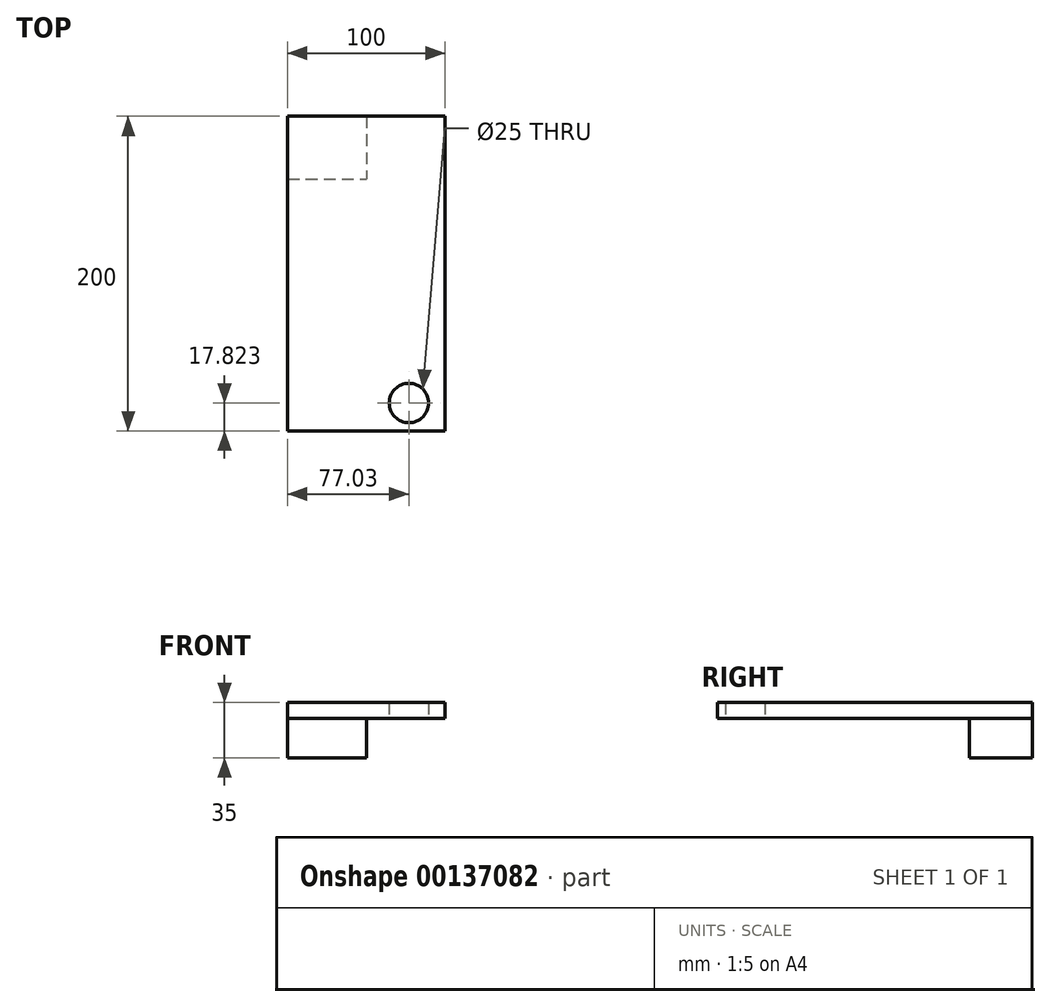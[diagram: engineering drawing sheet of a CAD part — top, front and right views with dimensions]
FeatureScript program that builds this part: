
annotation { "Feature Type Name" : "Feature", "Feature Type Description" : "" }
export const myFeature = defineFeature(function(context is Context, id is Id, definition is map)
    precondition{}
    {
        {
            var Q0;
            Q0=qCreatedBy(makeId("Top.planeOp"),FACE);
            var sketch = newSketch(context, id + "F0", { "sketchPlane" : qUnion([Q0])});
            skLineSegment(sketch, "E0.bottom", {"start": v(-74.4, 107.03) * mm, "end": v(25.6, 107.03) * mm});
            skLineSegment(sketch, "E0.top", {"start": v(-74.4, -92.97) * mm, "end": v(25.6, -92.97) * mm});
            skLineSegment(sketch, "E0.left", {"start": v(-74.4, 107.03) * mm, "end": v(-74.4, -92.97) * mm});
            skLineSegment(sketch, "E0.right", {"start": v(25.6, 107.03) * mm, "end": v(25.6, -92.97) * mm});
            skSolve(sketch);
        }
        {
            var Q0;
            Q0=makeQuery(id+"F0.imprint","IMPRINT",FACE,{"disambiguationData":[TD([[makeQuery(id+"F0.imprint","IMPRINT",EDGE,{"derivedFrom":sQuery(id+"F0.wireOp",EDGE,"E0.bottom")}),-1.0]])]});
            extrude(context, id + "F1", {"entities" : qUnion([Q0]), "depth" : 10 * mm});
        }
        {
            var Q0;
            Q0=makeQuery(id+"F1.opExtrude","CAP_FACE",FACE,{"disambiguationData":[OSD([sQuery(id+"F0.wireOp",EDGE,"E0.bottom"),sQuery(id+"F0.wireOp",EDGE,"E0.top"),sQuery(id+"F0.wireOp",EDGE,"E0.left"),sQuery(id+"F0.wireOp",EDGE,"E0.right")])],"isStart":true});
            var sketch = newSketch(context, id + "F2", { "sketchPlane" : qUnion([Q0])});
            skLineSegment(sketch, "E1.bottom", {"start": v(-74.4, -107.03) * mm, "end": v(-24.4, -107.03) * mm});
            skLineSegment(sketch, "E1.top", {"start": v(-74.4, -67.03) * mm, "end": v(-24.4, -67.03) * mm});
            skLineSegment(sketch, "E1.left", {"start": v(-74.4, -107.03) * mm, "end": v(-74.4, -67.03) * mm});
            skLineSegment(sketch, "E1.right", {"start": v(-24.4, -107.03) * mm, "end": v(-24.4, -67.03) * mm});
            skSolve(sketch);
        }
        {
            var Q0;
            Q0=makeQuery(id+"F2.imprint","IMPRINT",FACE,{"disambiguationData":[TD([[makeQuery(id+"F2.imprint","IMPRINT",EDGE,{"derivedFrom":sQuery(id+"F2.wireOp",EDGE,"E1.bottom")}),1.0]])]});
            extrude(context, id + "F3", {"entities" : qUnion([Q0]), "operationType" : NewBodyOperationType.ADD, "depth" : 25 * mm});
        }
        {
            var Q0;
            Q0=makeQuery(id+"F1.opExtrude","CAP_FACE",FACE,{"disambiguationData":[OSD([sQuery(id+"F0.wireOp",EDGE,"E0.bottom"),sQuery(id+"F0.wireOp",EDGE,"E0.top"),sQuery(id+"F0.wireOp",EDGE,"E0.left"),sQuery(id+"F0.wireOp",EDGE,"E0.right")])],"isStart":true});
            var sketch = newSketch(context, id + "F4", { "sketchPlane" : qUnion([Q0])});
            skCircle(sketch, "E2", {"center": v(2.63, 75.15) * mm, "radius": 12.5 * mm});
            skSolve(sketch);
        }
        {
            var Q0;
            Q0=makeQuery(id+"F4.imprint","IMPRINT",FACE,{"disambiguationData":[TD([[makeQuery(id+"F4.imprint","IMPRINT",EDGE,{"derivedFrom":sQuery(id+"F4.wireOp",EDGE,"E2")}),1.0]])]});
            extrude(context, id + "F5", {"entities" : qUnion([Q0]), "operationType" : NewBodyOperationType.REMOVE, "endBound" : BoundingType.THROUGH_ALL, "oppositeDirection" : true, "depth" : 25.4 * mm});
        }
    });
